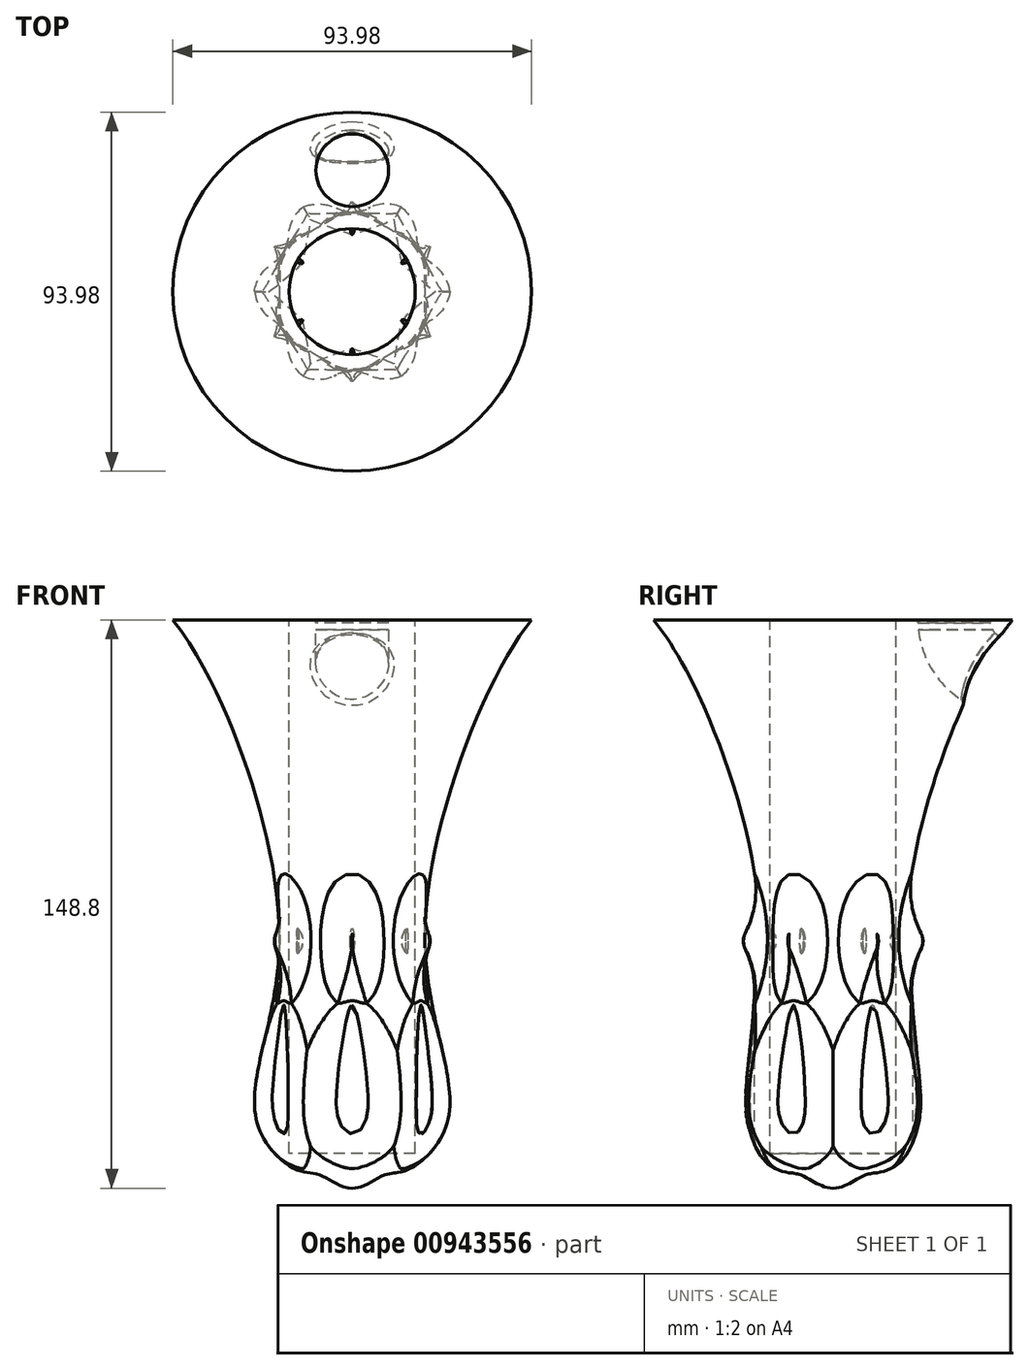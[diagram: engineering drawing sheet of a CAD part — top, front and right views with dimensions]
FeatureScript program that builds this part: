
annotation { "Feature Type Name" : "Feature", "Feature Type Description" : "" }
export const myFeature = defineFeature(function(context is Context, id is Id, definition is map)
    precondition{}
    {
        {
            var Q0;
            Q0=qCreatedBy(makeId("Front.planeOp"),FACE);
            var sketch = newSketch(context, id + "F0", { "sketchPlane" : qUnion([Q0])});
            skLineSegment(sketch, "E0", {"start": v(0, 0) * mm, "end": v(-16.51, 0) * mm});
            skLineSegment(sketch, "E1", {"start": v(-16.51, 0) * mm, "end": v(-16.51, 139.7) * mm});
            skLineSegment(sketch, "E2", {"start": v(-16.51, 139.7) * mm, "end": v(-47, 139.7) * mm});
            skPoint(sketch, "E3.4.internal.snap0", {"position": v(-8.26, 0) * mm});
            skFitSpline(sketch, "E3", {"points": [v(-47, 139.7) * mm, v(-19.1, 56.32) * mm, v(-25.28, 9.08) * mm, v(-14.37, -4.32) * mm, v(-8.26, -5.7) * mm, v(0, -9.1) * mm], "startDerivative": vector(103.36, -126) * mm, "endDerivative": vector(83.09, 0) * mm});
            skLineSegment(sketch, "E4", {"start": v(0, 0) * mm, "end": v(0, -9.1) * mm});
            skSolve(sketch);
        }
        {
            var Q0;
            Q0 = qSketchRegion(id + "F0", true);
            var Q1;
            Q1=sQuery(id+"F0.wireOp",EDGE,"E4");
            revolve(context, id + "F1", {"surfaceOperationType" : NewSurfaceOperationType.NEW, "entities" : qUnion([Q0]), "axis" : qUnion([Q1]), "revolveType" : RevolveType.FULL});
        }
        {
            var Q0;
            Q0=qCreatedBy(makeId("Top.planeOp"),FACE);
            var sketch = newSketch(context, id + "F2", { "sketchPlane" : qUnion([Q0])});
            skCircle(sketch, "E5", {"center": v(0, -29.76) * mm, "radius": 9 * mm});
            skCircle(sketch, "E6.1.0", {"center": v(25.77, -14.88) * mm, "radius": 9 * mm});
            skCircle(sketch, "E6.2.0", {"center": v(25.77, 14.88) * mm, "radius": 9 * mm});
            skCircle(sketch, "E6.3.0", {"center": v(0, 29.76) * mm, "radius": 9 * mm});
            skCircle(sketch, "E6.4.0", {"center": v(-25.77, 14.88) * mm, "radius": 9 * mm});
            skCircle(sketch, "E6.5.0", {"center": v(-25.77, -14.88) * mm, "radius": 9 * mm});
            skPoint(sketch, "E6.center", {"position": v(0, 0) * mm});
            skSolve(sketch);
        }
        {
            var Q0;
            Q0=makeQuery(id+"F2.imprint","IMPRINT",FACE,{"disambiguationData":[TD([[makeQuery(id+"F2.imprint","IMPRINT",EDGE,{"derivedFrom":sQuery(id+"F2.wireOp",EDGE,"E5")}),1.0]])]});
            var Q1;
            Q1=makeQuery(id+"F2.imprint","IMPRINT",FACE,{"disambiguationData":[TD([[makeQuery(id+"F2.imprint","IMPRINT",EDGE,{"derivedFrom":sQuery(id+"F2.wireOp",EDGE,"E6.1.0")}),1.0]])]});
            var Q2;
            Q2=makeQuery(id+"F2.imprint","IMPRINT",FACE,{"disambiguationData":[TD([[makeQuery(id+"F2.imprint","IMPRINT",EDGE,{"derivedFrom":sQuery(id+"F2.wireOp",EDGE,"E6.5.0")}),1.0]])]});
            var Q3;
            Q3=makeQuery(id+"F2.imprint","IMPRINT",FACE,{"disambiguationData":[TD([[makeQuery(id+"F2.imprint","IMPRINT",EDGE,{"derivedFrom":sQuery(id+"F2.wireOp",EDGE,"E6.4.0")}),1.0]])]});
            var Q4;
            Q4=makeQuery(id+"F2.imprint","IMPRINT",FACE,{"disambiguationData":[TD([[makeQuery(id+"F2.imprint","IMPRINT",EDGE,{"derivedFrom":sQuery(id+"F2.wireOp",EDGE,"E6.2.0")}),1.0]])]});
            var Q5;
            Q5=makeQuery(id+"F2.imprint","IMPRINT",FACE,{"disambiguationData":[TD([[makeQuery(id+"F2.imprint","IMPRINT",EDGE,{"derivedFrom":sQuery(id+"F2.wireOp",EDGE,"E6.3.0")}),1.0]])]});
            extrude(context, id + "F3", {"entities" : qUnion([Q0, Q1, Q2, Q3, Q4, Q5]), "operationType" : NewBodyOperationType.REMOVE, "depth" : 54.1 * mm, "offsetDistance" : 25.4 * mm});
        }
        {
            var Q0;
            Q0=makeQuery(id+"F3.boolean.opBoolean","COPY",FACE,{"derivedFrom":makeQuery(id+"F3.opExtrude","SWEPT_FACE",FACE,{"disambiguationData":[OSD([sQuery(id+"F2.wireOp",EDGE,"E5")])]})});
            var Q1;
            Q1=makeQuery(id+"F3.boolean.opBoolean","COPY",FACE,{"derivedFrom":makeQuery(id+"F3.opExtrude","SWEPT_FACE",FACE,{"disambiguationData":[OSD([sQuery(id+"F2.wireOp",EDGE,"E6.1.0")])]})});
            var Q2;
            Q2=makeQuery(id+"F3.boolean.opBoolean","COPY",FACE,{"derivedFrom":makeQuery(id+"F3.opExtrude","SWEPT_FACE",FACE,{"disambiguationData":[OSD([sQuery(id+"F2.wireOp",EDGE,"E6.2.0")])]})});
            var Q3;
            Q3=makeQuery(id+"F3.boolean.opBoolean","INTERSECT",EDGE,{"derivedFrom":[makeQuery(id+"F1.opRevolve","SWEPT_FACE",FACE,{"disambiguationData":[OSD([sQuery(id+"F0.wireOp",EDGE,"E3")])]}),makeQuery(id+"F3.opExtrude","SWEPT_FACE",FACE,{"disambiguationData":[OSD([sQuery(id+"F2.wireOp",EDGE,"E6.3.0")])]})]});
            var Q4;
            Q4=makeQuery(id+"F3.boolean.opBoolean","COPY",FACE,{"derivedFrom":makeQuery(id+"F3.opExtrude","SWEPT_FACE",FACE,{"disambiguationData":[OSD([sQuery(id+"F2.wireOp",EDGE,"E6.4.0")])]})});
            var Q5;
            Q5=makeQuery(id+"F3.boolean.opBoolean","COPY",FACE,{"derivedFrom":makeQuery(id+"F3.opExtrude","SWEPT_FACE",FACE,{"disambiguationData":[OSD([sQuery(id+"F2.wireOp",EDGE,"E6.5.0")])]})});
            fillet(context, id + "F4", {"entities" : qUnion([Q0, Q1, Q2, Q3, Q4, Q5]), "radius" : 10.16 * mm, "tangentPropagation" : true, "allowEdgeOverflow" : false});
        }
        {
            var Q0;
            Q0=qCreatedBy(makeId("Top.planeOp"),FACE);
            cPlane(context, id + "F5", {"entities" : qUnion([Q0]), "cplaneType" : CPlaneType.OFFSET, "offset" : 55.63 * mm, "width" : 152.4 * mm, "height" : 152.4 * mm});
        }
        {
            var Q0;
            Q0=qCreatedBy(id+"F5.planeOp",FACE);
            var sketch = newSketch(context, id + "F6", { "sketchPlane" : qUnion([Q0])});
            skEllipse(sketch, "E7", {"center": v(0, -19.24) * mm, "majorRadius": 4.3 * mm, "minorRadius": 0.73 * mm, "majorAxis": v(0, -1)});
            skEllipse(sketch, "E8.1.0", {"center": v(16.67, -9.62) * mm, "majorRadius": 4.3 * mm, "minorRadius": 0.73 * mm, "majorAxis": v(0.87, -0.5)});
            skEllipse(sketch, "E8.2.0", {"center": v(16.67, 9.62) * mm, "majorRadius": 4.3 * mm, "minorRadius": 0.73 * mm, "majorAxis": v(0.87, 0.5)});
            skEllipse(sketch, "E8.3.0", {"center": v(0, 19.24) * mm, "majorRadius": 4.3 * mm, "minorRadius": 0.73 * mm, "majorAxis": v(0, 1)});
            skEllipse(sketch, "E8.4.0", {"center": v(-16.67, 9.62) * mm, "majorRadius": 4.3 * mm, "minorRadius": 0.73 * mm, "majorAxis": v(-0.87, 0.5)});
            skEllipse(sketch, "E8.5.0", {"center": v(-16.67, -9.62) * mm, "majorRadius": 4.3 * mm, "minorRadius": 0.73 * mm, "majorAxis": v(-0.87, -0.5)});
            skPoint(sketch, "E8.center", {"position": v(0, 0) * mm});
            skLineSegment(sketch, "E9", {"start": v(-16.67, -9.62) * mm, "end": v(-16.3, -10.25) * mm});
            skLineSegment(sketch, "E10", {"start": v(-16.67, -9.62) * mm, "end": v(-17.03, -9) * mm});
            skLineSegment(sketch, "E11", {"start": v(0, -19.24) * mm, "end": v(-0.73, -19.24) * mm});
            skLineSegment(sketch, "E12", {"start": v(0, -19.24) * mm, "end": v(0.73, -19.24) * mm});
            skLineSegment(sketch, "E13", {"start": v(16.67, -9.62) * mm, "end": v(16.3, -10.25) * mm});
            skLineSegment(sketch, "E14", {"start": v(16.67, -9.62) * mm, "end": v(17.03, -9) * mm});
            skLineSegment(sketch, "E15", {"start": v(16.67, 9.62) * mm, "end": v(17.03, 9) * mm});
            skLineSegment(sketch, "E16", {"start": v(16.67, 9.62) * mm, "end": v(16.3, 10.25) * mm});
            skLineSegment(sketch, "E17", {"start": v(0, 19.24) * mm, "end": v(-0.73, 19.24) * mm});
            skLineSegment(sketch, "E18", {"start": v(0, 19.24) * mm, "end": v(0.73, 19.24) * mm});
            skLineSegment(sketch, "E19", {"start": v(-16.67, 9.62) * mm, "end": v(-17.03, 9) * mm});
            skLineSegment(sketch, "E20", {"start": v(-16.67, 9.62) * mm, "end": v(-16.3, 10.25) * mm});
            skSolve(sketch);
        }
        {
            var Q0;
            {var subQ0=sQuery(id+"F6.wireOp",EDGE,"E9");Q0=makeQuery(id+"F6.imprint","IMPRINT",FACE,{"disambiguationData":[TD([[makeQuery(id+"F6.imprint","IMPRINT",EDGE,{"derivedFrom":subQ0}),-1.0]])]});}
            var Q1;
            Q1=sQuery(id+"F6.wireOp",EDGE,"E9");
            revolve(context, id + "F7", {"operationType" : NewBodyOperationType.ADD, "surfaceOperationType" : NewSurfaceOperationType.NEW, "entities" : qUnion([Q0]), "axis" : qUnion([Q1]), "revolveType" : RevolveType.FULL});
        }
        {
            var Q0;
            {var subQ0=sQuery(id+"F6.wireOp",EDGE,"E11");Q0=makeQuery(id+"F6.imprint","IMPRINT",FACE,{"disambiguationData":[TD([[makeQuery(id+"F6.imprint","IMPRINT",EDGE,{"derivedFrom":subQ0}),1.0]])]});}
            var Q1;
            Q1=sQuery(id+"F6.wireOp",EDGE,"E12");
            revolve(context, id + "F8", {"operationType" : NewBodyOperationType.ADD, "surfaceOperationType" : NewSurfaceOperationType.NEW, "entities" : qUnion([Q0]), "axis" : qUnion([Q1]), "revolveType" : RevolveType.FULL});
        }
        {
            var Q0;
            {var subQ0=sQuery(id+"F6.wireOp",EDGE,"E13");Q0=makeQuery(id+"F6.imprint","IMPRINT",FACE,{"disambiguationData":[TD([[makeQuery(id+"F6.imprint","IMPRINT",EDGE,{"derivedFrom":subQ0}),-1.0]])]});}
            var Q1;
            Q1=sQuery(id+"F6.wireOp",EDGE,"E13");
            revolve(context, id + "F9", {"operationType" : NewBodyOperationType.ADD, "surfaceOperationType" : NewSurfaceOperationType.NEW, "entities" : qUnion([Q0]), "axis" : qUnion([Q1]), "revolveType" : RevolveType.FULL});
        }
        {
            var Q0;
            {var subQ0=sQuery(id+"F6.wireOp",EDGE,"E15");Q0=makeQuery(id+"F6.imprint","IMPRINT",FACE,{"disambiguationData":[TD([[makeQuery(id+"F6.imprint","IMPRINT",EDGE,{"derivedFrom":subQ0}),-1.0]])]});}
            var Q1;
            Q1=sQuery(id+"F6.wireOp",EDGE,"E16");
            revolve(context, id + "F10", {"operationType" : NewBodyOperationType.ADD, "surfaceOperationType" : NewSurfaceOperationType.NEW, "entities" : qUnion([Q0]), "axis" : qUnion([Q1]), "revolveType" : RevolveType.FULL});
        }
        {
            var Q0;
            {var subQ0=sQuery(id+"F6.wireOp",EDGE,"E17");Q0=makeQuery(id+"F6.imprint","IMPRINT",FACE,{"disambiguationData":[TD([[makeQuery(id+"F6.imprint","IMPRINT",EDGE,{"derivedFrom":subQ0}),1.0]])]});}
            var Q1;
            Q1=sQuery(id+"F6.wireOp",EDGE,"E17");
            revolve(context, id + "F11", {"operationType" : NewBodyOperationType.ADD, "surfaceOperationType" : NewSurfaceOperationType.NEW, "entities" : qUnion([Q0]), "axis" : qUnion([Q1]), "revolveType" : RevolveType.FULL});
        }
        {
            var Q0;
            {var subQ0=sQuery(id+"F6.wireOp",EDGE,"E19");Q0=makeQuery(id+"F6.imprint","IMPRINT",FACE,{"disambiguationData":[TD([[makeQuery(id+"F6.imprint","IMPRINT",EDGE,{"derivedFrom":subQ0}),1.0]])]});}
            var Q1;
            Q1=sQuery(id+"F6.wireOp",EDGE,"E20");
            revolve(context, id + "F12", {"operationType" : NewBodyOperationType.ADD, "surfaceOperationType" : NewSurfaceOperationType.NEW, "entities" : qUnion([Q0]), "axis" : qUnion([Q1]), "revolveType" : RevolveType.FULL});
        }
        {
            var Q0;
            Q0=makeQuery(id+"F7.boolean.opBoolean","INTERSECT",EDGE,{"derivedFrom":[makeQuery(id+"F4.opFillet","SPLIT",FACE,{"disambiguationData":[OD(1.0)],"derivedFrom":makeQuery(id+"F1.opRevolve","SWEPT_FACE",FACE,{"disambiguationData":[OSD([sQuery(id+"F0.wireOp",EDGE,"E3")])]})}),makeQuery(id+"F7.opRevolve","SWEPT_FACE",FACE,{"disambiguationData":[OSD([sQuery(id+"F6.wireOp",EDGE,"E8.5.0")])]})]});
            var Q1;
            Q1=makeQuery(id+"F8.boolean.opBoolean","INTERSECT",EDGE,{"derivedFrom":[makeQuery(id+"F4.opFillet","SPLIT",FACE,{"disambiguationData":[OD(1.0)],"derivedFrom":makeQuery(id+"F1.opRevolve","SWEPT_FACE",FACE,{"disambiguationData":[OSD([sQuery(id+"F0.wireOp",EDGE,"E3")])]})}),makeQuery(id+"F8.opRevolve","SWEPT_FACE",FACE,{"disambiguationData":[OSD([sQuery(id+"F6.wireOp",EDGE,"E7")])]})]});
            var Q2;
            Q2=makeQuery(id+"F9.boolean.opBoolean","INTERSECT",EDGE,{"derivedFrom":[makeQuery(id+"F4.opFillet","SPLIT",FACE,{"disambiguationData":[OD(1.0)],"derivedFrom":makeQuery(id+"F1.opRevolve","SWEPT_FACE",FACE,{"disambiguationData":[OSD([sQuery(id+"F0.wireOp",EDGE,"E3")])]})}),makeQuery(id+"F9.opRevolve","SWEPT_FACE",FACE,{"disambiguationData":[OSD([sQuery(id+"F6.wireOp",EDGE,"E8.1.0")])]})]});
            var Q3;
            Q3=makeQuery(id+"F10.boolean.opBoolean","INTERSECT",EDGE,{"derivedFrom":[makeQuery(id+"F4.opFillet","SPLIT",FACE,{"disambiguationData":[OD(1.0)],"derivedFrom":makeQuery(id+"F1.opRevolve","SWEPT_FACE",FACE,{"disambiguationData":[OSD([sQuery(id+"F0.wireOp",EDGE,"E3")])]})}),makeQuery(id+"F10.opRevolve","SWEPT_FACE",FACE,{"disambiguationData":[OSD([sQuery(id+"F6.wireOp",EDGE,"E8.2.0")])]})]});
            var Q4;
            Q4=makeQuery(id+"F11.boolean.opBoolean","INTERSECT",EDGE,{"derivedFrom":[makeQuery(id+"F4.opFillet","SPLIT",FACE,{"disambiguationData":[OD(1.0)],"derivedFrom":makeQuery(id+"F1.opRevolve","SWEPT_FACE",FACE,{"disambiguationData":[OSD([sQuery(id+"F0.wireOp",EDGE,"E3")])]})}),makeQuery(id+"F11.opRevolve","SWEPT_FACE",FACE,{"disambiguationData":[OSD([sQuery(id+"F6.wireOp",EDGE,"E8.3.0")])]})]});
            var Q5;
            Q5=makeQuery(id+"F12.boolean.opBoolean","INTERSECT",EDGE,{"derivedFrom":[makeQuery(id+"F4.opFillet","SPLIT",FACE,{"disambiguationData":[OD(1.0)],"derivedFrom":makeQuery(id+"F1.opRevolve","SWEPT_FACE",FACE,{"disambiguationData":[OSD([sQuery(id+"F0.wireOp",EDGE,"E3")])]})}),makeQuery(id+"F12.opRevolve","SWEPT_FACE",FACE,{"disambiguationData":[OSD([sQuery(id+"F6.wireOp",EDGE,"E8.4.0")])]})]});
            fillet(context, id + "F13", {"entities" : qUnion([Q0, Q1, Q2, Q3, Q4, Q5]), "radius" : 25.4 * mm, "tangentPropagation" : true, "allowEdgeOverflow" : false});
        }
        {
            var Q0;
            Q0=makeQuery(id+"F1.opRevolve","SWEPT_FACE",FACE,{"disambiguationData":[OSD([sQuery(id+"F0.wireOp",EDGE,"E2")])]});
            var sketch = newSketch(context, id + "F14", { "sketchPlane" : qUnion([Q0])});
            skLineSegment(sketch, "E21", {"start": v(0, 47) * mm, "end": v(0, 0) * mm});
            skLineSegment(sketch, "E22", {"start": v(0, 0) * mm, "end": v(0, 31.75) * mm});
            skCircle(sketch, "E23", {"center": v(0, 31.75) * mm, "radius": 9.53 * mm});
            skLineSegment(sketch, "E24", {"start": v(0, 47) * mm, "end": v(-12.82, 47) * mm});
            skSolve(sketch);
        }
        {
            var Q0;
            {var subQ0=sQuery(id+"F14.wireOp",EDGE,"E22");var subQ1=sQuery(id+"F14.wireOp",EDGE,"E21");var subQ2=makeQuery(id+"F14.imprint","INTERSECT",VERTEX,{"derivedFrom":[subQ1,subQ0]});Q0=makeQuery(id+"F14.imprint","IMPRINT",FACE,{"disambiguationData":[TD([[makeQuery(id+"F14.imprint","IMPRINT",EDGE,{"disambiguationData":[TD([[subQ2,1.0]])],"derivedFrom":subQ1}),-1.0]])]});}
            var Q1;
            {var subQ0=sQuery(id+"F14.wireOp",EDGE,"E22");var subQ1=sQuery(id+"F14.wireOp",EDGE,"E21");var subQ2=makeQuery(id+"F14.imprint","INTERSECT",VERTEX,{"derivedFrom":[subQ1,subQ0]});Q1=makeQuery(id+"F14.imprint","IMPRINT",FACE,{"disambiguationData":[TD([[makeQuery(id+"F14.imprint","IMPRINT",EDGE,{"disambiguationData":[TD([[subQ2,1.0]])],"derivedFrom":subQ1}),1.0]])]});}
            var Q2;
            Q2=sQuery(id+"F14.wireOp",EDGE,"E24");
            revolve(context, id + "F15", {"operationType" : NewBodyOperationType.REMOVE, "surfaceOperationType" : NewSurfaceOperationType.NEW, "entities" : qUnion([Q0, Q1]), "axis" : qUnion([Q2]), "revolveType" : RevolveType.FULL, "oppositeDirection" : true});
        }
        {
            var Q0;
            Q0=makeQuery(id+"F15.boolean.opBoolean","INTERSECT",EDGE,{"derivedFrom":[makeQuery(id+"F4.opFillet","SPLIT",FACE,{"disambiguationData":[OD(1.0)],"derivedFrom":makeQuery(id+"F1.opRevolve","SWEPT_FACE",FACE,{"disambiguationData":[OSD([sQuery(id+"F0.wireOp",EDGE,"E3")])]})}),makeQuery(id+"F15.opRevolve","SWEPT_FACE",FACE,{"disambiguationData":[OSD([sQuery(id+"F14.wireOp",EDGE,"E23")])]})]});
            fillet(context, id + "F16", {"entities" : qUnion([Q0]), "radius" : 1.27 * mm, "tangentPropagation" : true, "allowEdgeOverflow" : false});
        }
        {
            var Q0;
            Q0=makeQuery(id+"F1.opRevolve","SWEPT_FACE",FACE,{"disambiguationData":[OSD([sQuery(id+"F0.wireOp",EDGE,"E2")])]});
            var sketch = newSketch(context, id + "F17", { "sketchPlane" : qUnion([Q0])});
            skCircle(sketch, "E25", {"center": v(0, 31.75) * mm, "radius": 10.31 * mm});
            skSolve(sketch);
        }
        {
            var Q0;
            Q0 = qSketchRegion(id + "F17", true);
            extrude(context, id + "F18", {"entities" : qUnion([Q0]), "operationType" : NewBodyOperationType.ADD, "oppositeDirection" : true, "depth" : 2.54 * mm, "offsetDistance" : 25.4 * mm});
        }
        {
            var Q0;
            Q0=makeQuery(id+"F17.imprint","IMPRINT",FACE,{"disambiguationData":[TD([[makeQuery(id+"F17.imprint","IMPRINT",EDGE,{"derivedFrom":makeQuery(id+"F15.boolean.opBoolean","INTERSECT",EDGE,{"derivedFrom":[makeQuery(id+"F1.opRevolve","SWEPT_FACE",FACE,{"disambiguationData":[OSD([sQuery(id+"F0.wireOp",EDGE,"E2")])]}),makeQuery(id+"F15.opRevolve","SWEPT_FACE",FACE,{"disambiguationData":[OSD([sQuery(id+"F14.wireOp",EDGE,"E23")])]})]})}),1.0]])]});
            var sketch = newSketch(context, id + "F19", { "sketchPlane" : qUnion([Q0])});
            skLineSegment(sketch, "E26", {"start": v(0, 0) * mm, "end": v(0, 31.75) * mm});
            skCircle(sketch, "E27", {"center": v(0, 31.75) * mm, "radius": 9.53 * mm});
            skSolve(sketch);
        }
        {
            var Q0;
            Q0=makeQuery(id+"F19.imprint","IMPRINT",FACE,{"disambiguationData":[TD([[makeQuery(id+"F19.imprint","IMPRINT",EDGE,{"derivedFrom":sQuery(id+"F19.wireOp",EDGE,"E27")}),1.0]])]});
            extrude(context, id + "F20", {"entities" : qUnion([Q0]), "operationType" : NewBodyOperationType.REMOVE, "oppositeDirection" : true, "depth" : 0.76 * mm, "offsetDistance" : 25.4 * mm});
        }
    });
